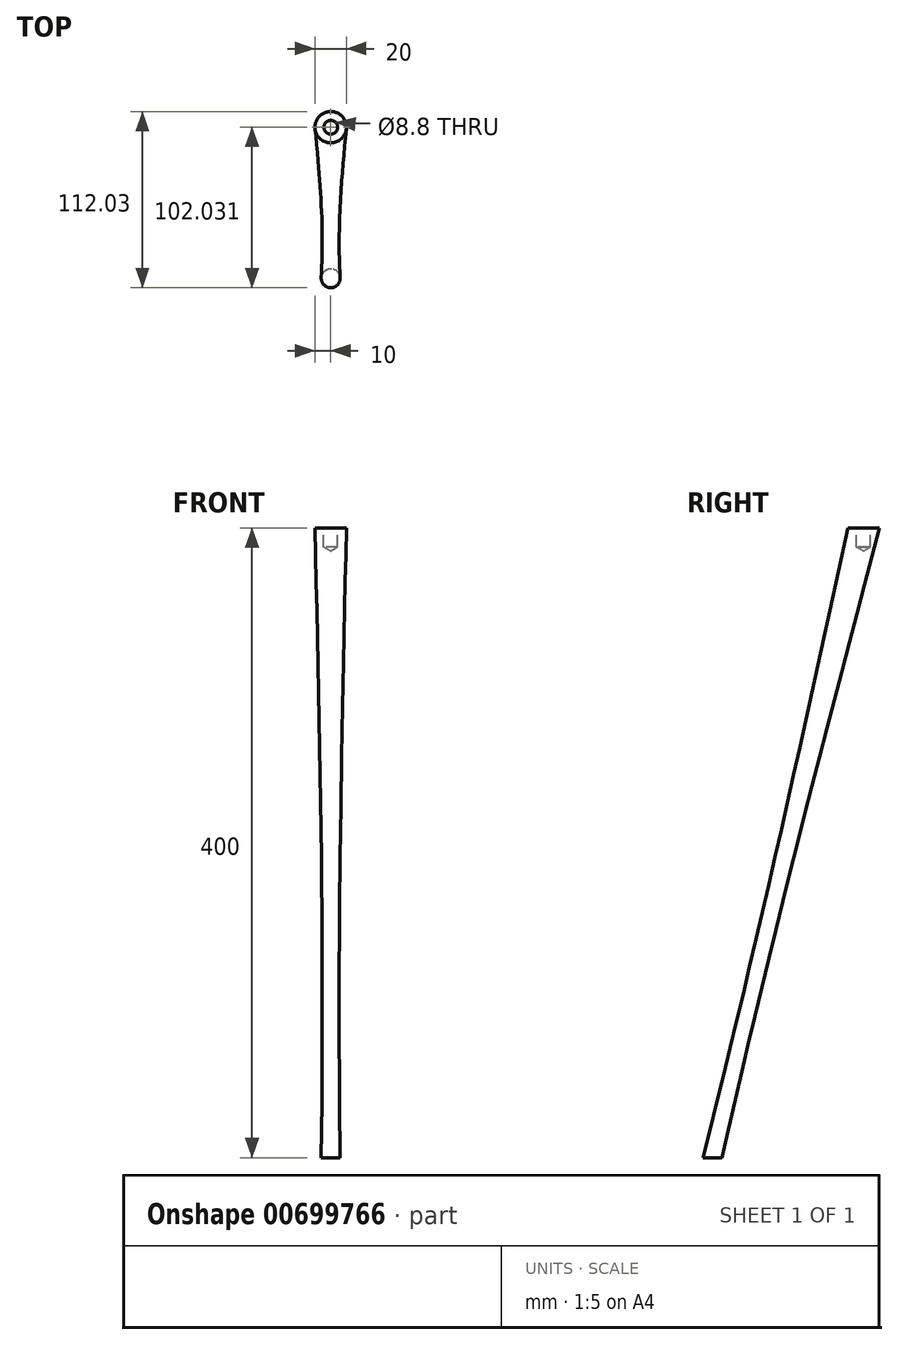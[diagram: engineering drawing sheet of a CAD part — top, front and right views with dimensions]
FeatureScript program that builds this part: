
annotation { "Feature Type Name" : "Feature", "Feature Type Description" : "" }
export const myFeature = defineFeature(function(context is Context, id is Id, definition is map)
    precondition{}
    {
        {
            var Q0;
            Q0=qCreatedBy(makeId("Top.planeOp"),FACE);
            var sketch = newSketch(context, id + "F0", { "sketchPlane" : qUnion([Q0])});
            skCircle(sketch, "E0", {"center": v(0, 0) * mm, "radius": 6 * mm});
            skSolve(sketch);
        }
        {
            var Q0;
            Q0=qCreatedBy(makeId("Right.planeOp"),FACE);
            var sketch = newSketch(context, id + "F1", { "sketchPlane" : qUnion([Q0])});
            skLineSegment(sketch, "E1", {"start": v(0, 0) * mm, "end": v(96.03, 400) * mm});
            skSolve(sketch);
        }
        {
            var Q0;
            Q0=sQuery(id+"F1.wireOp",VERTEX,"E1.end");
            var Q1;
            Q1=qCreatedBy(makeId("Top.planeOp"),FACE);
            cPlane(context, id + "F2", {"entities" : qUnion([Q0, Q1]), "cplaneType" : CPlaneType.PLANE_POINT, "offset" : 25 * mm, "width" : 150 * mm, "height" : 150 * mm});
        }
        {
            var Q0;
            Q0=qCreatedBy(id+"F2.planeOp",FACE);
            var sketch = newSketch(context, id + "F3", { "sketchPlane" : qUnion([Q0])});
            skCircle(sketch, "E2", {"center": v(0, 96.03) * mm, "radius": 10 * mm});
            skSolve(sketch);
        }
        {
            var Q0;
            Q0=makeQuery(id+"F3.imprint","IMPRINT",FACE,{"disambiguationData":[TD([[makeQuery(id+"F3.imprint","IMPRINT",EDGE,{"derivedFrom":sQuery(id+"F3.wireOp",EDGE,"E2")}),1.0]])]});
            var Q1;
            Q1=makeQuery(id+"F0.imprint","IMPRINT",FACE,{"disambiguationData":[TD([[makeQuery(id+"F0.imprint","IMPRINT",EDGE,{"derivedFrom":sQuery(id+"F0.wireOp",EDGE,"E0")}),1.0]])]});
            loft(context, id + "F4", {"sheetProfilesArray" : [{ "sheetProfileEntities" : qUnion([Q0]) }, { "sheetProfileEntities" : qUnion([Q1]) }]});
        }
        {
            var Q0;
            Q0=makeQuery(id+"F4.opLoft","CAP_FACE",FACE,{"disambiguationData":[OSD([makeQuery(id+"F3.imprint","IMPRINT",FACE,{"disambiguationData":[TD([[makeQuery(id+"F3.imprint","IMPRINT",EDGE,{"derivedFrom":sQuery(id+"F3.wireOp",EDGE,"E2")}),1.0]])]})])],"isStart":true});
            var sketch = newSketch(context, id + "F5", { "sketchPlane" : qUnion([Q0])});
            skPoint(sketch, "E3", {"position": v(0, 96.03) * mm});
            skSolve(sketch);
        }
        {
            var Q0;
            Q0=sQuery(id+"F5.wireOp",VERTEX,"E3");
            var Q1;
            Q1=makeQuery(id+"F4.opLoft","SWEPT_BODY",BODY,{"disambiguationData":[OSD([makeQuery(id+"F0.imprint","IMPRINT",FACE,{"disambiguationData":[TD([[makeQuery(id+"F0.imprint","IMPRINT",EDGE,{"derivedFrom":sQuery(id+"F0.wireOp",EDGE,"E0")}),1.0]])]}),makeQuery(id+"F3.imprint","IMPRINT",FACE,{"disambiguationData":[TD([[makeQuery(id+"F3.imprint","IMPRINT",EDGE,{"derivedFrom":sQuery(id+"F3.wireOp",EDGE,"E2")}),1.0]])]})])]});
            hole(context, id + "F6", {"style" : HoleStyle.SIMPLE, "endStyle" : HoleEndStyle.BLIND, "standardTappedOrClearance" : lookupTablePath({ "standard" : "ISO", "fit" : "Normal", "size" : "M8", "type" : "Clearance" }), "standardBlindInLast" : lookupTablePath({ "fit" : "Standard", "standard" : "ISO", "size" : "M8", "type" : "Clearance" }), "holeDiameter" : 8.8 * mm, "majorDiameter" : 5 * mm, "holeDepth" : 12 * mm, "isTappedThrough" : true, "tappedDepth" : 12 * mm, "tapClearance" : 3, "locations" : qUnion([Q0]), "scope" : qUnion([Q1])});
        }
    });
